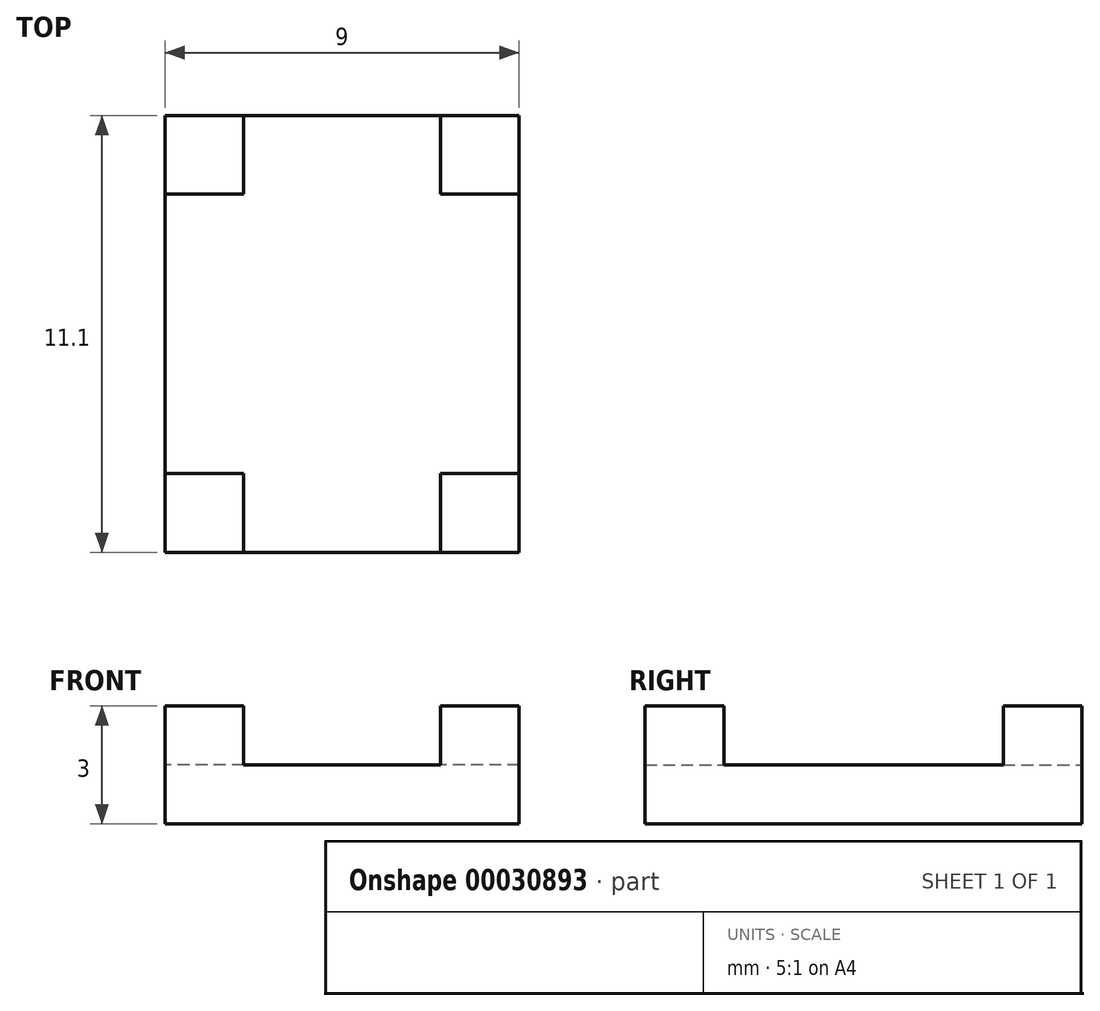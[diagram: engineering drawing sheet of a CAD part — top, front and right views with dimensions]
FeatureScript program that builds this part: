
annotation { "Feature Type Name" : "Feature", "Feature Type Description" : "" }
export const myFeature = defineFeature(function(context is Context, id is Id, definition is map)
    precondition{}
    {
        {
            var Q0;
            Q0=qCreatedBy(makeId("Top.planeOp"),FACE);
            var sketch = newSketch(context, id + "F0", { "sketchPlane" : qUnion([Q0])});
            skLineSegment(sketch, "E0.bottom", {"start": v(4.5, -6.05) * mm, "end": v(-4.5, -6.05) * mm});
            skLineSegment(sketch, "E0.top", {"start": v(4.5, 5.05) * mm, "end": v(-4.5, 5.05) * mm});
            skLineSegment(sketch, "E0.left", {"start": v(4.5, -6.05) * mm, "end": v(4.5, 5.05) * mm});
            skLineSegment(sketch, "E0.right", {"start": v(-4.5, -6.05) * mm, "end": v(-4.5, 5.05) * mm});
            skLineSegment(sketch, "E1.bottom", {"start": v(2, -2.55) * mm, "end": v(-2, -2.55) * mm, "construction": true});
            skLineSegment(sketch, "E1.top", {"start": v(2, 2.55) * mm, "end": v(-2, 2.55) * mm, "construction": true});
            skLineSegment(sketch, "E1.left", {"start": v(2, -2.55) * mm, "end": v(2, 2.55) * mm, "construction": true});
            skLineSegment(sketch, "E1.right", {"start": v(-2, -2.55) * mm, "end": v(-2, 2.55) * mm, "construction": true});
            skLineSegment(sketch, "E2.bottom", {"start": v(-2, 1.55) * mm, "end": v(-6, 1.55) * mm, "construction": true});
            skLineSegment(sketch, "E2.top", {"start": v(-2, -3.55) * mm, "end": v(-6, -3.55) * mm, "construction": true});
            skLineSegment(sketch, "E2.left", {"start": v(-2, 1.55) * mm, "end": v(-2, -3.55) * mm, "construction": true});
            skLineSegment(sketch, "E2.right", {"start": v(-6, 1.55) * mm, "end": v(-6, -3.55) * mm, "construction": true});
            skSolve(sketch);
        }
        {
            var Q0;
            Q0 = qSketchRegion(id + "F0", true);
            extrude(context, id + "F1", {"entities" : qUnion([Q0]), "depth" : 1.5 * mm});
        }
        {
            var Q0;
            Q0=makeQuery(id+"F1.opExtrude","CAP_FACE",FACE,{"disambiguationData":[OSD([sQuery(id+"F0.wireOp",EDGE,"E0.bottom"),sQuery(id+"F0.wireOp",EDGE,"E0.top"),sQuery(id+"F0.wireOp",EDGE,"E0.left"),sQuery(id+"F0.wireOp",EDGE,"E0.right")])],"isStart":false});
            var sketch = newSketch(context, id + "F2", { "sketchPlane" : qUnion([Q0])});
            skLineSegment(sketch, "E3.bottom", {"start": v(-2.5, 3.05) * mm, "end": v(-4.5, 3.05) * mm});
            skLineSegment(sketch, "E3.top", {"start": v(-2.5, 5.05) * mm, "end": v(-4.5, 5.05) * mm});
            skLineSegment(sketch, "E3.left", {"start": v(-2.5, 3.05) * mm, "end": v(-2.5, 5.05) * mm});
            skLineSegment(sketch, "E3.right", {"start": v(-4.5, 3.05) * mm, "end": v(-4.5, 5.05) * mm});
            skLineSegment(sketch, "E4.0.1.0", {"start": v(-2.5, -6.05) * mm, "end": v(-2.5, -4.05) * mm});
            skLineSegment(sketch, "E4.0.1.1", {"start": v(-2.5, -6.05) * mm, "end": v(-4.5, -6.05) * mm});
            skLineSegment(sketch, "E4.0.1.2", {"start": v(-4.5, -6.05) * mm, "end": v(-4.5, -4.05) * mm});
            skLineSegment(sketch, "E4.0.1.3", {"start": v(-2.5, -4.05) * mm, "end": v(-4.5, -4.05) * mm});
            skLineSegment(sketch, "E4.1.0.0", {"start": v(4.5, 3.05) * mm, "end": v(4.5, 5.05) * mm});
            skLineSegment(sketch, "E4.1.0.1", {"start": v(4.5, 3.05) * mm, "end": v(2.5, 3.05) * mm});
            skLineSegment(sketch, "E4.1.0.2", {"start": v(2.5, 3.05) * mm, "end": v(2.5, 5.05) * mm});
            skLineSegment(sketch, "E4.1.0.3", {"start": v(4.5, 5.05) * mm, "end": v(2.5, 5.05) * mm});
            skLineSegment(sketch, "E4.1.1.0", {"start": v(4.5, -6.05) * mm, "end": v(4.5, -4.05) * mm});
            skLineSegment(sketch, "E4.1.1.1", {"start": v(4.5, -6.05) * mm, "end": v(2.5, -6.05) * mm});
            skLineSegment(sketch, "E4.1.1.2", {"start": v(2.5, -6.05) * mm, "end": v(2.5, -4.05) * mm});
            skLineSegment(sketch, "E4.1.1.3", {"start": v(4.5, -4.05) * mm, "end": v(2.5, -4.05) * mm});
            skLineSegment(sketch, "E4.direction1", {"start": v(-2.5, 3.05) * mm, "end": v(4.5, 3.05) * mm, "construction": true});
            skLineSegment(sketch, "E4.direction2", {"start": v(-2.5, 3.05) * mm, "end": v(-2.5, -6.05) * mm, "construction": true});
            skSolve(sketch);
        }
        {
            var Q0;
            Q0 = qSketchRegion(id + "F2", true);
            extrude(context, id + "F3", {"entities" : qUnion([Q0]), "operationType" : NewBodyOperationType.ADD, "depth" : 1.5 * mm});
        }
    });
